# Revit family: NBS_WallgateLtd_UndrmntdWshBsns_VBU-01
name_source: partatom
category: Plumbing Fixtures
revit_build: Autodesk Revit 2014 (Build: 20130709_2115(x64)
units: mm (PartAtom-declared; Revit-internal decimal feet)

## types (1)
- VBU-01
    AssetType = Fixed
    BIMObjectName = NBS_WallgateLtd_UndermountedWashBasins_VBU-01
    ColourOptions = MA - Thames, MAH - Frost, MAW - White, MC - Bluestone, MCA - Aubergine, MCB - Diamantina, MCC - Black, MCD - Orange, MCE - Pink, MO - Slate, MS - Hyco, MCJ - Light Grey, MCF - NHS Blue
    Description = Anti-ligature, anti-vandal solid surface undermount bowl, with a secure bottom oulet waste
    DrainSize = 32 mm
    Durability = Compliant to Grade 5
    DurationUnit = year
    Features = Hygienic and easily cleaned, highly vandal-resistant, anti-ligature
    IfcExportAs = IfcSanitaryTerminalType
    IfcExportType = WASHHANDBASIN
    IntegralAccessoryOptions = BWN Deck Mounted Basin Water Nozzle, ALT Deck Mounted Tap, WT38 Tap Ware, WDC Electronic Controllers, PBA Piezo Touch Buttons, PBA-IR Infra-Red Activation Sensors, WVPV Vanity Water Valve Pack, ALT-100 Wall Mounted Nozzle, VT1000/2000/3000 Vanity Tops, MV0001 Thermostatic Mixer Valve
    ManufacturerName = Wallgate Ltd
    ManufacturerURL = www.wallgate.com
    Material = High-grade solid surface
    ModelNumber = VBU-01
    NBSCertification = www.nationalbimlibrary.com/cert/alfiola3
    NBSDescription = Undermounted wash basins
    NBSReference = 45-35-70/366
    Name = UndermoutedWashBasins_VBU-01_WallgateLtd
    NominalDepth = 404 mm
    NominalHeight = 175 mm
    NominalLength = 0 mm  [stored 0 ft]
    NominalWidth = 485 mm
    ProductInformation = www.wallgate.com/document-centre/docmenu-wash-basins/doccat-washbasins-undermount/622-vbu-01-installation-drawing-undermounted-bowl-for-vanity-top/file
    Size = 485 x 404 x 175 mm
    Uniclass2 = 45-31-79/492
    Version = 3
    WarrantyDurationParts = 1
    WarrantyDurationUnit = year
    WashBasinMaterial = NBS_Concept
    WashHandBasinMounting = CounterTop
    WashHandBasinType = Vanity
    Weight = 7.3 kg

note: [stored X ft] marks values corroborated as IEEE doubles in the binary element streams (Revit-internal decimal feet)

## geometry (parser evidence)
native form markers: Sweep x1
no freeform markers — native parametric forms only
